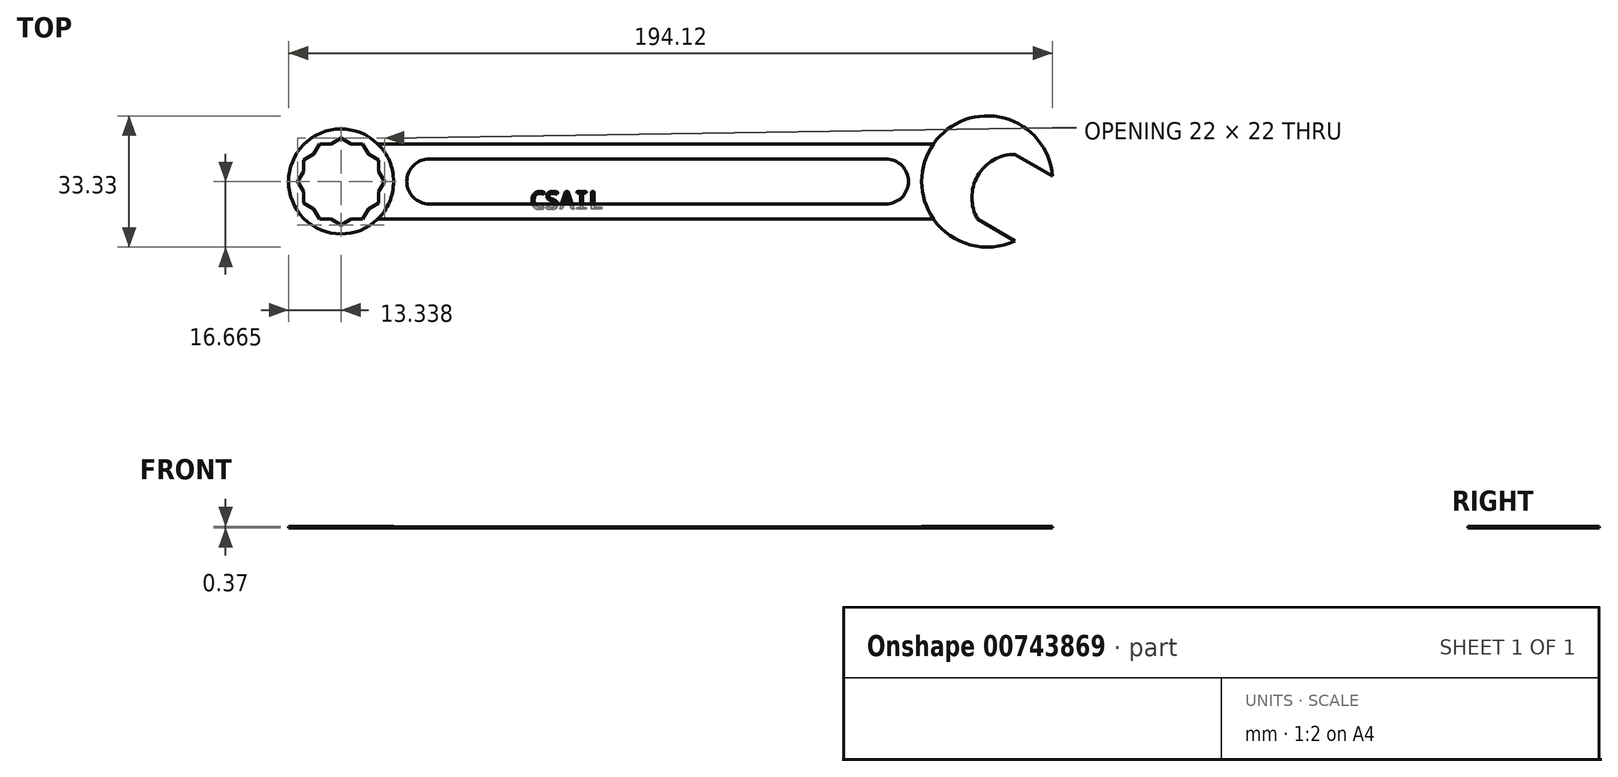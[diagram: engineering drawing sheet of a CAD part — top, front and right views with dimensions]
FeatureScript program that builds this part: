
annotation { "Feature Type Name" : "Feature", "Feature Type Description" : "" }
export const myFeature = defineFeature(function(context is Context, id is Id, definition is map)
    precondition{}
    {
        {
            assignVariable(context, id + "F0", {"name" : "handlethickness", "anyValue" : 1 / 4});
        }
        {
            assignVariable(context, id + "F1", {"name" : "wrenchthick", "anyValue" : 1 / 8});
        }
        {
            assignVariable(context, id + "F2", {"name" : "slotdepth", "anyValue" : .15});
        }
        {
            var Q0;
            Q0=qCreatedBy(makeId("Top.planeOp"),FACE);
            var sketch = newSketch(context, id + "F3", { "sketchPlane" : qUnion([Q0])});
            skLineSegment(sketch, "E0.bottom", {"start": v(0, 0) * mm, "end": v(152.4, 0) * mm});
            skLineSegment(sketch, "E0.top", {"start": v(0, 19.05) * mm, "end": v(152.4, 19.05) * mm});
            skLineSegment(sketch, "E0.left", {"start": v(0, 0) * mm, "end": v(0, 19.05) * mm});
            skLineSegment(sketch, "E0.right", {"start": v(152.4, 0) * mm, "end": v(152.4, 19.05) * mm});
            skSolve(sketch);
        }
        {
            var Q0;
            Q0=makeQuery(id+"F3.imprint","IMPRINT",FACE,{"disambiguationData":[TD([[makeQuery(id+"F3.imprint","IMPRINT",EDGE,{"derivedFrom":sQuery(id+"F3.wireOp",EDGE,"E0.bottom")}),1.0]])]});
            extrude(context, id + "F4", {"entities" : qUnion([Q0]), "flatOperationType" : FlatOperationType.REMOVE, "depth" : (getVariable(context, 'handlethickness')) * mm, "offsetDistance" : 25.4 * mm, "domain" : OperationDomain.MODEL});
        }
        {
            var Q0;
            Q0=makeQuery(id+"F4.opExtrude","CAP_FACE",FACE,{"disambiguationData":[OSD([sQuery(id+"F3.wireOp",EDGE,"E0.bottom"),sQuery(id+"F3.wireOp",EDGE,"E0.top"),sQuery(id+"F3.wireOp",EDGE,"E0.left"),sQuery(id+"F3.wireOp",EDGE,"E0.right")])],"isStart":false});
            var Q1;
            Q1=makeQuery(id+"F4.opExtrude","CAP_FACE",FACE,{"disambiguationData":[OSD([sQuery(id+"F3.wireOp",EDGE,"E0.bottom"),sQuery(id+"F3.wireOp",EDGE,"E0.top"),sQuery(id+"F3.wireOp",EDGE,"E0.left"),sQuery(id+"F3.wireOp",EDGE,"E0.right")])],"isStart":true});
            cPlane(context, id + "F5", {"entities" : qUnion([Q0, Q1]), "cplaneType" : CPlaneType.MID_PLANE, "offset" : 25.4 * mm, "width" : 152.4 * mm, "height" : 152.4 * mm});
        }
        {
            var Q0;
            Q0=qCreatedBy(id+"F5.planeOp",FACE);
            var sketch = newSketch(context, id + "F6", { "sketchPlane" : qUnion([Q0])});
            skPoint(sketch, "E1.0", {"position": v(152.4, 19.05) * mm});
            skCircle(sketch, "E2", {"center": v(154.84, 9.53) * mm, "radius": 16.67 * mm});
            skPoint(sketch, "E2.third.point", {"position": v(171.32, 7.01) * mm});
            skCircle(sketch, "E3.cCircle", {"center": v(161.93, 5.44) * mm, "radius": 9.53 * mm, "construction": true});
            skLineSegment(sketch, "E3.0", {"start": v(171.45, -0.06) * mm, "end": v(161.92, -5.56) * mm});
            skLineSegment(sketch, "E3.1", {"start": v(161.92, -5.56) * mm, "end": v(152.4, -0.06) * mm});
            skLineSegment(sketch, "E3.2", {"start": v(152.4, -0.06) * mm, "end": v(152.4, 10.93) * mm});
            skLineSegment(sketch, "E3.3", {"start": v(152.4, 10.93) * mm, "end": v(161.93, 16.43) * mm});
            skLineSegment(sketch, "E3.4", {"start": v(161.93, 16.43) * mm, "end": v(171.45, 10.93) * mm});
            skLineSegment(sketch, "E3.5", {"start": v(171.45, 10.93) * mm, "end": v(171.45, -0.06) * mm});
            skPoint(sketch, "E3.0.midPoint", {"position": v(166.69, -2.81) * mm});
            skPoint(sketch, "E4.0", {"position": v(152.4, 9.53) * mm});
            skArc(sketch, "E5", {"start": v(161.93, 16.43) * mm, "mid": v(152.4, 10.93) * mm, "end": v(152.4, -0.06) * mm});
            skLineSegment(sketch, "E6.0.1", {"start": v(0, 19.05) * mm, "end": v(0, 0) * mm, "construction": true});
            skPoint(sketch, "E7", {"position": v(141.16, 0) * mm});
            skPoint(sketch, "E8", {"position": v(139.1, 4.06) * mm});
            skPoint(sketch, "E9.0", {"position": v(152.4, 0) * mm});
            skLineSegment(sketch, "E10.0", {"start": v(152.4, 0) * mm, "end": v(152.4, 19.05) * mm, "construction": true});
            skSolve(sketch);
        }
        {
            var Q0;
            {var subQ5=sQuery(id+"F6.wireOp",EDGE,"E3.1");Q0=makeQuery(id+"F6.imprint","IMPRINT",FACE,{"disambiguationData":[TD([[makeQuery(id+"F6.imprint","IMPRINT",EDGE,{"derivedFrom":subQ5}),1.0]])]});}
            extrude(context, id + "F7", {"entities" : qUnion([Q0]), "operationType" : NewBodyOperationType.ADD, "depth" : (getVariable(context, 'handlethickness') + getVariable(context, 'wrenchthick')) * mm, "offsetDistance" : 25.4 * mm, "symmetric" : true});
        }
        {
            var Q0;
            Q0=qCreatedBy(id+"F5.planeOp",FACE);
            var sketch = newSketch(context, id + "F8", { "sketchPlane" : qUnion([Q0])});
            skPoint(sketch, "E11.0", {"position": v(0, 19.05) * mm});
            skPoint(sketch, "E12.0", {"position": v(0, 0) * mm});
            skPoint(sketch, "E13.0", {"position": v(0, 9.53) * mm});
            skCircle(sketch, "E14", {"center": v(-9.33, 9.53) * mm, "radius": 13.33 * mm});
            skPoint(sketch, "E14.third.point", {"position": v(-17.92, 19.72) * mm});
            skCircle(sketch, "E15.cCircle", {"center": v(-9.33, 9.53) * mm, "radius": 9.53 * mm, "construction": true});
            skLineSegment(sketch, "E15.0", {"start": v(-20.33, 9.53) * mm, "end": v(-14.83, 19.05) * mm});
            skLineSegment(sketch, "E15.1", {"start": v(-14.83, 19.05) * mm, "end": v(-3.83, 19.05) * mm});
            skLineSegment(sketch, "E15.2", {"start": v(-3.83, 19.05) * mm, "end": v(1.67, 9.53) * mm});
            skLineSegment(sketch, "E15.3", {"start": v(1.67, 9.53) * mm, "end": v(-3.83, 0) * mm});
            skLineSegment(sketch, "E15.4", {"start": v(-3.83, 0) * mm, "end": v(-14.83, 0) * mm});
            skLineSegment(sketch, "E15.5", {"start": v(-14.83, 0) * mm, "end": v(-20.33, 9.53) * mm});
            skPoint(sketch, "E15.0.midPoint", {"position": v(-17.58, 14.29) * mm});
            skLineSegment(sketch, "E16.0", {"start": v(-9.33, 20.52) * mm, "end": v(0.2, 15.02) * mm});
            skLineSegment(sketch, "E16.1", {"start": v(0.2, 15.02) * mm, "end": v(0.2, 4.03) * mm});
            skLineSegment(sketch, "E16.2", {"start": v(0.2, 4.03) * mm, "end": v(-9.33, -1.47) * mm});
            skLineSegment(sketch, "E16.3", {"start": v(-9.33, -1.47) * mm, "end": v(-18.86, 4.03) * mm});
            skLineSegment(sketch, "E16.4", {"start": v(-18.86, 4.03) * mm, "end": v(-18.86, 15.02) * mm});
            skLineSegment(sketch, "E16.5", {"start": v(-18.86, 15.02) * mm, "end": v(-9.33, 20.52) * mm});
            skPoint(sketch, "E16.0.midPoint", {"position": v(-4.57, 17.77) * mm});
            skSolve(sketch);
        }
        {
            var Q0;
            Q0 = qSketchRegion(id + "F8", true);
            extrude(context, id + "F9", {"entities" : qUnion([Q0]), "operationType" : NewBodyOperationType.ADD, "depth" : (getVariable(context, 'wrenchthick') + getVariable(context, 'handlethickness')) * mm, "offsetDistance" : 25.4 * mm, "symmetric" : true});
        }
        {
            var Q0;
            {var subQ0=sQuery(id+"F3.wireOp",EDGE,"E0.bottom");var subQ1=sQuery(id+"F3.wireOp",EDGE,"E0.top");Q0=makeQuery(id+"F9.boolean.opBoolean","SPLIT",FACE,{"disambiguationData":[TD([makeQuery(id+"F4.opExtrude","SWEPT_FACE",FACE,{"disambiguationData":[OSD([subQ0])]})])],"derivedFrom":makeQuery(id+"F4.opExtrude","CAP_FACE",FACE,{"disambiguationData":[OSD([subQ0,subQ1,sQuery(id+"F3.wireOp",EDGE,"E0.left"),sQuery(id+"F3.wireOp",EDGE,"E0.right")])],"isStart":false})});}
            var sketch = newSketch(context, id + "F10", { "sketchPlane" : qUnion([Q0])});
            skLineSegment(sketch, "E17", {"start": v(4, 9.53) * mm, "end": v(138.17, 9.53) * mm, "construction": true});
            skLineSegment(sketch, "E18.bottom", {"start": v(13.08, 3.81) * mm, "end": v(129.1, 3.81) * mm});
            skLineSegment(sketch, "E18.top", {"start": v(13.08, 15.24) * mm, "end": v(129.1, 15.24) * mm});
            skLineSegment(sketch, "E18.left", {"start": v(13.08, 3.81) * mm, "end": v(13.08, 15.24) * mm});
            skLineSegment(sketch, "E18.right", {"start": v(129.1, 3.81) * mm, "end": v(129.1, 15.24) * mm});
            skPoint(sketch, "E18.middle", {"position": v(71.09, 9.53) * mm});
            skCircle(sketch, "E19", {"center": v(13.08, 9.53) * mm, "radius": 5.72 * mm});
            skCircle(sketch, "E20", {"center": v(129.1, 9.53) * mm, "radius": 5.71 * mm});
            skSolve(sketch);
        }
        {
            var Q0;
            {var subQ0=sQuery(id+"F10.wireOp",EDGE,"E18.left");Q0=makeQuery(id+"F10.imprint","IMPRINT",FACE,{"disambiguationData":[TD([[makeQuery(id+"F10.imprint","IMPRINT",EDGE,{"derivedFrom":subQ0}),1.0]])]});}
            var Q1;
            {var subQ0=sQuery(id+"F10.wireOp",EDGE,"E18.right");Q1=makeQuery(id+"F10.imprint","IMPRINT",FACE,{"disambiguationData":[TD([[makeQuery(id+"F10.imprint","IMPRINT",EDGE,{"derivedFrom":subQ0}),-1.0]])]});}
            var Q2;
            {var subQ0=sQuery(id+"F10.wireOp",EDGE,"E18.bottom");Q2=makeQuery(id+"F10.imprint","IMPRINT",FACE,{"disambiguationData":[TD([[makeQuery(id+"F10.imprint","IMPRINT",EDGE,{"derivedFrom":subQ0}),1.0]])]});}
            var Q3;
            {var subQ0=sQuery(id+"F10.wireOp",EDGE,"E18.right");Q3=makeQuery(id+"F10.imprint","IMPRINT",FACE,{"disambiguationData":[TD([[makeQuery(id+"F10.imprint","IMPRINT",EDGE,{"derivedFrom":subQ0}),1.0]])]});}
            var Q4;
            {var subQ0=sQuery(id+"F10.wireOp",EDGE,"E18.left");Q4=makeQuery(id+"F10.imprint","IMPRINT",FACE,{"disambiguationData":[TD([[makeQuery(id+"F10.imprint","IMPRINT",EDGE,{"derivedFrom":subQ0}),-1.0]])]});}
            extrude(context, id + "F11", {"entities" : qUnion([Q0, Q1, Q2, Q3, Q4]), "operationType" : NewBodyOperationType.REMOVE, "oppositeDirection" : true, "depth" : (getVariable(context, 'slotdepth')) * mm, "offsetDistance" : 25.4 * mm});
        }
        {
            var Q0;
            Q0=makeQuery(id+"F11.boolean.opBoolean","COPY",FACE,{"derivedFrom":makeQuery(id+"F11.opExtrude","CAP_FACE",FACE,{"disambiguationData":[OSD([sQuery(id+"F10.wireOp",EDGE,"E18.bottom"),sQuery(id+"F10.wireOp",EDGE,"E18.top"),sQuery(id+"F10.wireOp",EDGE,"E19"),sQuery(id+"F10.wireOp",EDGE,"E20")])],"isStart":false})});
            var sketch = newSketch(context, id + "F12", { "sketchPlane" : qUnion([Q0])});
            skText(sketch, "E21", { "text": "CSAIL", "fontName": "DroidSansMono.ttf"});
            skPoint(sketch, "E22.0", {"position": v(71.09, 15.24) * mm});
            skPoint(sketch, "E23.0", {"position": v(134.8, 9.53) * mm});
            skLineSegment(sketch, "E24", {"start": v(49.92, 9.53) * mm, "end": v(92.26, 9.53) * mm, "construction": true});
            const initialGuessF12  = {"E21": [0.03875, 0.00253, 1, 0, 0.00446]};
            skSetInitialGuess(sketch, initialGuessF12);
            skSolve(sketch);
        }
        {
            var Q0;
            Q0 = qSketchRegion(id + "F12", true);
            extrude(context, id + "F13", {"entities" : qUnion([Q0]), "operationType" : NewBodyOperationType.REMOVE, "oppositeDirection" : true, "depth" : (getVariable(context, 'slotdepth') * .2) * mm, "offsetDistance" : 25.4 * mm});
        }
        {
            var Q0;
            Q0=makeQuery(id+"F11.boolean.opBoolean","COPY",EDGE,{"derivedFrom":makeQuery(id+"F11.opExtrude","CAP_EDGE",EDGE,{"disambiguationData":[OSD([sQuery(id+"F10.wireOp",EDGE,"E20")])],"isStart":true})});
            var Q1;
            Q1=makeQuery(id+"F11.boolean.opBoolean","COPY",EDGE,{"derivedFrom":makeQuery(id+"F11.opExtrude","CAP_EDGE",EDGE,{"disambiguationData":[OSD([sQuery(id+"F10.wireOp",EDGE,"E18.top")])],"isStart":true})});
            var Q2;
            Q2=makeQuery(id+"F11.boolean.opBoolean","COPY",EDGE,{"derivedFrom":makeQuery(id+"F11.opExtrude","CAP_EDGE",EDGE,{"disambiguationData":[OSD([sQuery(id+"F10.wireOp",EDGE,"E19")])],"isStart":true})});
            var Q3;
            Q3=makeQuery(id+"F11.boolean.opBoolean","COPY",EDGE,{"derivedFrom":makeQuery(id+"F11.opExtrude","CAP_EDGE",EDGE,{"disambiguationData":[OSD([sQuery(id+"F10.wireOp",EDGE,"E18.bottom")])],"isStart":true})});
            var Q4;
            Q4=makeQuery(id+"F11.boolean.opBoolean","COPY",EDGE,{"derivedFrom":makeQuery(id+"F11.opExtrude","CAP_EDGE",EDGE,{"disambiguationData":[OSD([sQuery(id+"F10.wireOp",EDGE,"E18.bottom")])],"isStart":false})});
            var Q5;
            Q5=makeQuery(id+"F11.boolean.opBoolean","COPY",EDGE,{"derivedFrom":makeQuery(id+"F11.opExtrude","CAP_EDGE",EDGE,{"disambiguationData":[OSD([sQuery(id+"F10.wireOp",EDGE,"E20")])],"isStart":false})});
            var Q6;
            Q6=makeQuery(id+"F11.boolean.opBoolean","COPY",EDGE,{"derivedFrom":makeQuery(id+"F11.opExtrude","CAP_EDGE",EDGE,{"disambiguationData":[OSD([sQuery(id+"F10.wireOp",EDGE,"E19")])],"isStart":false})});
            var Q7;
            Q7=makeQuery(id+"F11.boolean.opBoolean","COPY",EDGE,{"derivedFrom":makeQuery(id+"F11.opExtrude","CAP_EDGE",EDGE,{"disambiguationData":[OSD([sQuery(id+"F10.wireOp",EDGE,"E18.top")])],"isStart":false})});
            fillet(context, id + "F14", {"entities" : qUnion([Q0, Q1, Q2, Q3, Q4, Q5, Q6, Q7]), "radius" : (getVariable(context, 'slotdepth') * .5) * mm, "tangentPropagation" : true, "allowEdgeOverflow" : false});
        }
        {
            var Q0;
            Q0=makeQuery(id+"F4.opExtrude","SWEPT_EDGE",EDGE,{"disambiguationData":[OSD([sQuery(id+"F3.wireOp",EDGE,"E0.bottom"),sQuery(id+"F3.wireOp",EDGE,"E0.left")])]});
            var Q1;
            Q1=makeQuery(id+"F9.boolean.opBoolean","INTERSECT",EDGE,{"derivedFrom":[makeQuery(id+"F4.opExtrude","CAP_FACE",FACE,{"disambiguationData":[OSD([sQuery(id+"F3.wireOp",EDGE,"E0.bottom"),sQuery(id+"F3.wireOp",EDGE,"E0.top"),sQuery(id+"F3.wireOp",EDGE,"E0.left"),sQuery(id+"F3.wireOp",EDGE,"E0.right")])],"isStart":false}),makeQuery(id+"F9.opExtrude","SWEPT_FACE",FACE,{"disambiguationData":[OSD([sQuery(id+"F8.wireOp",EDGE,"E14")])]})]});
            var Q2;
            Q2=makeQuery(id+"F4.opExtrude","SWEPT_EDGE",EDGE,{"disambiguationData":[OSD([sQuery(id+"F3.wireOp",EDGE,"E0.top"),sQuery(id+"F3.wireOp",EDGE,"E0.left")])]});
            var Q3;
            Q3=makeQuery(id+"F4.opExtrude","SWEPT_EDGE",EDGE,{"disambiguationData":[OSD([sQuery(id+"F3.wireOp",EDGE,"E0.top"),sQuery(id+"F3.wireOp",EDGE,"E0.right")])]});
            var Q4;
            Q4=makeQuery(id+"F7.boolean.opBoolean","INTERSECT",EDGE,{"derivedFrom":[makeQuery(id+"F4.opExtrude","CAP_FACE",FACE,{"disambiguationData":[OSD([sQuery(id+"F3.wireOp",EDGE,"E0.bottom"),sQuery(id+"F3.wireOp",EDGE,"E0.top"),sQuery(id+"F3.wireOp",EDGE,"E0.left"),sQuery(id+"F3.wireOp",EDGE,"E0.right")])],"isStart":true}),makeQuery(id+"F7.opExtrude","SWEPT_FACE",FACE,{"disambiguationData":[OSD([sQuery(id+"F6.wireOp",EDGE,"E2")])]})]});
            var Q5;
            Q5=makeQuery(id+"F7.boolean.opBoolean","INTERSECT",EDGE,{"derivedFrom":[makeQuery(id+"F4.opExtrude","CAP_FACE",FACE,{"disambiguationData":[OSD([sQuery(id+"F3.wireOp",EDGE,"E0.bottom"),sQuery(id+"F3.wireOp",EDGE,"E0.top"),sQuery(id+"F3.wireOp",EDGE,"E0.left"),sQuery(id+"F3.wireOp",EDGE,"E0.right")])],"isStart":false}),makeQuery(id+"F7.opExtrude","SWEPT_FACE",FACE,{"disambiguationData":[OSD([sQuery(id+"F6.wireOp",EDGE,"E2")])]})]});
            var Q6;
            Q6=makeQuery(id+"F4.opExtrude","SWEPT_EDGE",EDGE,{"disambiguationData":[OSD([sQuery(id+"F3.wireOp",EDGE,"E0.bottom"),sQuery(id+"F3.wireOp",EDGE,"E0.right")])]});
            var Q7;
            Q7=makeQuery(id+"F9.boolean.opBoolean","INTERSECT",EDGE,{"derivedFrom":[makeQuery(id+"F4.opExtrude","CAP_FACE",FACE,{"disambiguationData":[OSD([sQuery(id+"F3.wireOp",EDGE,"E0.bottom"),sQuery(id+"F3.wireOp",EDGE,"E0.top"),sQuery(id+"F3.wireOp",EDGE,"E0.left"),sQuery(id+"F3.wireOp",EDGE,"E0.right")])],"isStart":true}),makeQuery(id+"F9.opExtrude","SWEPT_FACE",FACE,{"disambiguationData":[OSD([sQuery(id+"F8.wireOp",EDGE,"E14")])]})]});
            var Q8;
            Q8=makeQuery(id+"F7.boolean.opBoolean","INTERSECT",EDGE,{"derivedFrom":[makeQuery(id+"F4.opExtrude","SWEPT_FACE",FACE,{"disambiguationData":[OSD([sQuery(id+"F3.wireOp",EDGE,"E0.bottom")])]}),makeQuery(id+"F7.opExtrude","SWEPT_FACE",FACE,{"disambiguationData":[OSD([sQuery(id+"F6.wireOp",EDGE,"E2")])]})]});
            var Q9;
            Q9=makeQuery(id+"F7.boolean.opBoolean","INTERSECT",EDGE,{"derivedFrom":[makeQuery(id+"F4.opExtrude","SWEPT_FACE",FACE,{"disambiguationData":[OSD([sQuery(id+"F3.wireOp",EDGE,"E0.top")])]}),makeQuery(id+"F7.opExtrude","SWEPT_FACE",FACE,{"disambiguationData":[OSD([sQuery(id+"F6.wireOp",EDGE,"E2")])]})]});
            fillet(context, id + "F15", {"entities" : qUnion([Q0, Q1, Q2, Q3, Q4, Q5, Q6, Q7, Q8, Q9]), "radius" : (getVariable(context, 'handlethickness') / 2) * mm, "tangentPropagation" : true, "allowEdgeOverflow" : false});
        }
        {
            var Q0;
            {var subQ7=sQuery(id+"F3.wireOp",EDGE,"E0.left");Q0=makeQuery(id+"F9.boolean.opBoolean","SPLIT",FACE,{"disambiguationData":[TD([makeQuery(id+"F4.opExtrude","SWEPT_FACE",FACE,{"disambiguationData":[OSD([subQ7])]})])],"derivedFrom":makeQuery(id+"F4.opExtrude","CAP_FACE",FACE,{"disambiguationData":[OSD([sQuery(id+"F3.wireOp",EDGE,"E0.bottom"),sQuery(id+"F3.wireOp",EDGE,"E0.top"),subQ7,sQuery(id+"F3.wireOp",EDGE,"E0.right")])],"isStart":false})});}
            var sketch = newSketch(context, id + "F16", { "sketchPlane" : qUnion([Q0])});
            skLineSegment(sketch, "E25.0.0", {"start": v(0, 15.14) * mm, "end": v(0, 3.91) * mm});
            skLineSegment(sketch, "E25.0.1", {"start": v(0, 3.91) * mm, "end": v(0.2, 4.03) * mm});
            skLineSegment(sketch, "E25.0.2", {"start": v(0.2, 4.03) * mm, "end": v(0.2, 6.97) * mm});
            skLineSegment(sketch, "E25.0.3", {"start": v(0.2, 6.97) * mm, "end": v(1.67, 9.53) * mm});
            skLineSegment(sketch, "E25.0.4", {"start": v(1.67, 9.53) * mm, "end": v(0.2, 12.08) * mm});
            skLineSegment(sketch, "E25.0.5", {"start": v(0.2, 12.08) * mm, "end": v(0.2, 15.02) * mm});
            skLineSegment(sketch, "E25.0.6", {"start": v(0.2, 15.02) * mm, "end": v(0, 15.14) * mm});
            skSolve(sketch);
        }
        {
            var Q0;
            Q0 = qSketchRegion(id + "F16", true);
            extrude(context, id + "F17", {"entities" : qUnion([Q0]), "operationType" : NewBodyOperationType.REMOVE, "endBound" : BoundingType.THROUGH_ALL, "oppositeDirection" : true, "depth" : 25.4 * mm, "offsetDistance" : 25.4 * mm});
        }
        {
            var Q0;
            {var subQ0=sQuery(id+"F3.wireOp",EDGE,"E0.bottom");var subQ1=sQuery(id+"F3.wireOp",EDGE,"E0.right");Q0=makeQuery(id+"F7.boolean.opBoolean","SPLIT",FACE,{"disambiguationData":[TD([makeQuery(id+"F4.opExtrude","SWEPT_FACE",FACE,{"disambiguationData":[OSD([subQ1])]})])],"derivedFrom":makeQuery(id+"F4.opExtrude","CAP_FACE",FACE,{"disambiguationData":[OSD([subQ0,sQuery(id+"F3.wireOp",EDGE,"E0.top"),sQuery(id+"F3.wireOp",EDGE,"E0.left"),subQ1])],"isStart":false})});}
            var sketch = newSketch(context, id + "F18", { "sketchPlane" : qUnion([Q0])});
            skArc(sketch, "E26.0.0", {"start": v(152.36, 0) * mm, "mid": v(150.93, 5.47) * mm, "end": v(152.4, 10.93) * mm});
            skArc(sketch, "E26.0.1", {"start": v(152.36, 0) * mm, "mid": v(152.4, 0.24) * mm, "end": v(152.4, 0.48) * mm});
            skLineSegment(sketch, "E26.0.2", {"start": v(152.4, 0.48) * mm, "end": v(152.4, 10.93) * mm});
            skSolve(sketch);
        }
        {
            var Q0;
            Q0=makeQuery(id+"F18.imprint","IMPRINT",FACE,{"disambiguationData":[TD([[makeQuery(id+"F18.imprint","IMPRINT",EDGE,{"derivedFrom":sQuery(id+"F18.wireOp",EDGE,"E26.0.0")}),-1.0]])]});
            extrude(context, id + "F19", {"entities" : qUnion([Q0]), "operationType" : NewBodyOperationType.REMOVE, "endBound" : BoundingType.THROUGH_ALL, "oppositeDirection" : true, "depth" : 25.4 * mm, "offsetDistance" : 25.4 * mm});
        }
        {
            var Q0;
            Q0=makeQuery(id+"F13.boolean.opBoolean","COPY",EDGE,{"derivedFrom":makeQuery(id+"F13.opExtrude","CAP_EDGE",EDGE,{"disambiguationData":[OSD([sQuery(id+"F12.wireOp",EDGE,"E21.sketch_text.stroke-4")])],"isStart":true})});
            var Q1;
            Q1=makeQuery(id+"F13.boolean.opBoolean","COPY",EDGE,{"derivedFrom":makeQuery(id+"F13.opExtrude","CAP_EDGE",EDGE,{"disambiguationData":[OSD([sQuery(id+"F12.wireOp",EDGE,"E21.sketch_text.stroke-5")])],"isStart":true})});
            var Q2;
            Q2=makeQuery(id+"F13.boolean.opBoolean","COPY",EDGE,{"derivedFrom":makeQuery(id+"F13.opExtrude","CAP_EDGE",EDGE,{"disambiguationData":[OSD([sQuery(id+"F12.wireOp",EDGE,"E21.sketch_text.stroke-6")])],"isStart":false})});
            var Q3;
            Q3=makeQuery(id+"F13.boolean.opBoolean","COPY",EDGE,{"derivedFrom":makeQuery(id+"F13.opExtrude","CAP_EDGE",EDGE,{"disambiguationData":[OSD([sQuery(id+"F12.wireOp",EDGE,"E21.sketch_text.stroke-8")])],"isStart":true})});
            var Q4;
            Q4=makeQuery(id+"F13.boolean.opBoolean","COPY",EDGE,{"derivedFrom":makeQuery(id+"F13.opExtrude","CAP_EDGE",EDGE,{"disambiguationData":[OSD([sQuery(id+"F12.wireOp",EDGE,"E21.sketch_text.stroke-7")])],"isStart":true})});
            var Q5;
            Q5=makeQuery(id+"F13.boolean.opBoolean","COPY",EDGE,{"derivedFrom":makeQuery(id+"F13.opExtrude","CAP_EDGE",EDGE,{"disambiguationData":[OSD([sQuery(id+"F12.wireOp",EDGE,"E21.sketch_text.stroke-9")])],"isStart":true})});
            var Q6;
            Q6=makeQuery(id+"F13.boolean.opBoolean","COPY",EDGE,{"derivedFrom":makeQuery(id+"F13.opExtrude","CAP_EDGE",EDGE,{"disambiguationData":[OSD([sQuery(id+"F12.wireOp",EDGE,"E21.sketch_text.stroke-10")])],"isStart":true})});
            var Q7;
            Q7=makeQuery(id+"F13.boolean.opBoolean","COPY",EDGE,{"derivedFrom":makeQuery(id+"F13.opExtrude","CAP_EDGE",EDGE,{"disambiguationData":[OSD([sQuery(id+"F12.wireOp",EDGE,"E21.sketch_text.stroke-12")])],"isStart":false})});
            var Q8;
            Q8=makeQuery(id+"F13.boolean.opBoolean","COPY",EDGE,{"derivedFrom":makeQuery(id+"F13.opExtrude","CAP_EDGE",EDGE,{"disambiguationData":[OSD([sQuery(id+"F12.wireOp",EDGE,"E21.sketch_text.stroke-11")])],"isStart":true})});
            var Q9;
            Q9=makeQuery(id+"F13.boolean.opBoolean","COPY",EDGE,{"derivedFrom":makeQuery(id+"F13.opExtrude","CAP_EDGE",EDGE,{"disambiguationData":[OSD([sQuery(id+"F12.wireOp",EDGE,"E21.sketch_text.stroke-13")])],"isStart":false})});
            var Q10;
            Q10=makeQuery(id+"F13.boolean.opBoolean","COPY",EDGE,{"derivedFrom":makeQuery(id+"F13.opExtrude","CAP_EDGE",EDGE,{"disambiguationData":[OSD([sQuery(id+"F12.wireOp",EDGE,"E21.sketch_text.stroke-12")])],"isStart":true})});
            var Q11;
            Q11=makeQuery(id+"F13.boolean.opBoolean","COPY",EDGE,{"derivedFrom":makeQuery(id+"F13.opExtrude","CAP_EDGE",EDGE,{"disambiguationData":[OSD([sQuery(id+"F12.wireOp",EDGE,"E21.sketch_text.stroke-13")])],"isStart":true})});
            var Q12;
            Q12=makeQuery(id+"F13.boolean.opBoolean","COPY",EDGE,{"derivedFrom":makeQuery(id+"F13.opExtrude","CAP_EDGE",EDGE,{"disambiguationData":[OSD([sQuery(id+"F12.wireOp",EDGE,"E21.sketch_text.stroke-0")])],"isStart":true})});
            var Q13;
            Q13=makeQuery(id+"F13.boolean.opBoolean","COPY",EDGE,{"derivedFrom":makeQuery(id+"F13.opExtrude","CAP_EDGE",EDGE,{"disambiguationData":[OSD([sQuery(id+"F12.wireOp",EDGE,"E21.sketch_text.stroke-0")])],"isStart":false})});
            var Q14;
            Q14=makeQuery(id+"F13.boolean.opBoolean","COPY",EDGE,{"derivedFrom":makeQuery(id+"F13.opExtrude","CAP_EDGE",EDGE,{"disambiguationData":[OSD([sQuery(id+"F12.wireOp",EDGE,"E21.sketch_text.stroke-1")])],"isStart":true})});
            var Q15;
            Q15=makeQuery(id+"F13.boolean.opBoolean","COPY",EDGE,{"derivedFrom":makeQuery(id+"F13.opExtrude","CAP_EDGE",EDGE,{"disambiguationData":[OSD([sQuery(id+"F12.wireOp",EDGE,"E21.sketch_text.stroke-2")])],"isStart":true})});
            var Q16;
            Q16=makeQuery(id+"F13.boolean.opBoolean","COPY",EDGE,{"derivedFrom":makeQuery(id+"F13.opExtrude","CAP_EDGE",EDGE,{"disambiguationData":[OSD([sQuery(id+"F12.wireOp",EDGE,"E21.sketch_text.stroke-11")])],"isStart":false})});
            var Q17;
            Q17=makeQuery(id+"F13.boolean.opBoolean","COPY",EDGE,{"derivedFrom":makeQuery(id+"F13.opExtrude","CAP_EDGE",EDGE,{"disambiguationData":[OSD([sQuery(id+"F12.wireOp",EDGE,"E21.sketch_text.stroke-10")])],"isStart":false})});
            var Q18;
            Q18=makeQuery(id+"F13.boolean.opBoolean","COPY",EDGE,{"derivedFrom":makeQuery(id+"F13.opExtrude","CAP_EDGE",EDGE,{"disambiguationData":[OSD([sQuery(id+"F12.wireOp",EDGE,"E21.sketch_text.stroke-3")])],"isStart":true})});
            var Q19;
            Q19=makeQuery(id+"F13.boolean.opBoolean","COPY",EDGE,{"derivedFrom":makeQuery(id+"F13.opExtrude","CAP_EDGE",EDGE,{"disambiguationData":[OSD([sQuery(id+"F12.wireOp",EDGE,"E21.sketch_text.stroke-9")])],"isStart":false})});
            var Q20;
            Q20=makeQuery(id+"F13.boolean.opBoolean","COPY",EDGE,{"derivedFrom":makeQuery(id+"F13.opExtrude","CAP_EDGE",EDGE,{"disambiguationData":[OSD([sQuery(id+"F12.wireOp",EDGE,"E21.sketch_text.stroke-5")])],"isStart":false})});
            var Q21;
            Q21=makeQuery(id+"F13.boolean.opBoolean","COPY",EDGE,{"derivedFrom":makeQuery(id+"F13.opExtrude","CAP_EDGE",EDGE,{"disambiguationData":[OSD([sQuery(id+"F12.wireOp",EDGE,"E21.sketch_text.stroke-6")])],"isStart":true})});
            var Q22;
            Q22=makeQuery(id+"F13.boolean.opBoolean","COPY",EDGE,{"derivedFrom":makeQuery(id+"F13.opExtrude","CAP_EDGE",EDGE,{"disambiguationData":[OSD([sQuery(id+"F12.wireOp",EDGE,"E21.sketch_text.stroke-7")])],"isStart":false})});
            var Q23;
            Q23=makeQuery(id+"F13.boolean.opBoolean","COPY",EDGE,{"derivedFrom":makeQuery(id+"F13.opExtrude","CAP_EDGE",EDGE,{"disambiguationData":[OSD([sQuery(id+"F12.wireOp",EDGE,"E21.sketch_text.stroke-4")])],"isStart":false})});
            var Q24;
            Q24=makeQuery(id+"F13.boolean.opBoolean","COPY",EDGE,{"derivedFrom":makeQuery(id+"F13.opExtrude","CAP_EDGE",EDGE,{"disambiguationData":[OSD([sQuery(id+"F12.wireOp",EDGE,"E21.sketch_text.stroke-3")])],"isStart":false})});
            var Q25;
            Q25=makeQuery(id+"F13.boolean.opBoolean","COPY",EDGE,{"derivedFrom":makeQuery(id+"F13.opExtrude","CAP_EDGE",EDGE,{"disambiguationData":[OSD([sQuery(id+"F12.wireOp",EDGE,"E21.sketch_text.stroke-2")])],"isStart":false})});
            var Q26;
            Q26=makeQuery(id+"F13.boolean.opBoolean","COPY",EDGE,{"derivedFrom":makeQuery(id+"F13.opExtrude","CAP_EDGE",EDGE,{"disambiguationData":[OSD([sQuery(id+"F12.wireOp",EDGE,"E21.sketch_text.stroke-1")])],"isStart":false})});
            var Q27;
            Q27=makeQuery(id+"F13.boolean.opBoolean","COPY",EDGE,{"derivedFrom":makeQuery(id+"F13.opExtrude","CAP_EDGE",EDGE,{"disambiguationData":[OSD([sQuery(id+"F12.wireOp",EDGE,"E21.sketch_text.stroke-8")])],"isStart":false})});
            var Q28;
            Q28=makeQuery(id+"F13.boolean.opBoolean","COPY",EDGE,{"derivedFrom":makeQuery(id+"F13.opExtrude","CAP_EDGE",EDGE,{"disambiguationData":[OSD([sQuery(id+"F12.wireOp",EDGE,"E21.sketch_text.stroke-15")])],"isStart":true})});
            var Q29;
            Q29=makeQuery(id+"F13.boolean.opBoolean","COPY",EDGE,{"derivedFrom":makeQuery(id+"F13.opExtrude","CAP_EDGE",EDGE,{"disambiguationData":[OSD([sQuery(id+"F12.wireOp",EDGE,"E21.sketch_text.stroke-16")])],"isStart":true})});
            var Q30;
            Q30=makeQuery(id+"F13.boolean.opBoolean","COPY",EDGE,{"derivedFrom":makeQuery(id+"F13.opExtrude","CAP_EDGE",EDGE,{"disambiguationData":[OSD([sQuery(id+"F12.wireOp",EDGE,"E21.sketch_text.stroke-15")])],"isStart":false})});
            var Q31;
            Q31=makeQuery(id+"F13.boolean.opBoolean","COPY",EDGE,{"derivedFrom":makeQuery(id+"F13.opExtrude","CAP_EDGE",EDGE,{"disambiguationData":[OSD([sQuery(id+"F12.wireOp",EDGE,"E21.sketch_text.stroke-16")])],"isStart":false})});
            var Q32;
            Q32=makeQuery(id+"F13.boolean.opBoolean","COPY",EDGE,{"derivedFrom":makeQuery(id+"F13.opExtrude","CAP_EDGE",EDGE,{"disambiguationData":[OSD([sQuery(id+"F12.wireOp",EDGE,"E21.sketch_text.stroke-14")])],"isStart":false})});
            var Q33;
            Q33=makeQuery(id+"F13.boolean.opBoolean","COPY",EDGE,{"derivedFrom":makeQuery(id+"F13.opExtrude","CAP_EDGE",EDGE,{"disambiguationData":[OSD([sQuery(id+"F12.wireOp",EDGE,"E21.sketch_text.stroke-14")])],"isStart":true})});
            var Q34;
            Q34=makeQuery(id+"F13.boolean.opBoolean","COPY",EDGE,{"derivedFrom":makeQuery(id+"F13.opExtrude","CAP_EDGE",EDGE,{"disambiguationData":[OSD([sQuery(id+"F12.wireOp",EDGE,"E21.sketch_text.stroke-33")])],"isStart":true})});
            var Q35;
            Q35=makeQuery(id+"F13.boolean.opBoolean","COPY",EDGE,{"derivedFrom":makeQuery(id+"F13.opExtrude","CAP_EDGE",EDGE,{"disambiguationData":[OSD([sQuery(id+"F12.wireOp",EDGE,"E21.sketch_text.stroke-33")])],"isStart":false})});
            var Q36;
            Q36=makeQuery(id+"F13.boolean.opBoolean","COPY",EDGE,{"derivedFrom":makeQuery(id+"F13.opExtrude","CAP_EDGE",EDGE,{"disambiguationData":[OSD([sQuery(id+"F12.wireOp",EDGE,"E21.sketch_text.stroke-32")])],"isStart":false})});
            var Q37;
            Q37=makeQuery(id+"F13.boolean.opBoolean","COPY",EDGE,{"derivedFrom":makeQuery(id+"F13.opExtrude","CAP_EDGE",EDGE,{"disambiguationData":[OSD([sQuery(id+"F12.wireOp",EDGE,"E21.sketch_text.stroke-32")])],"isStart":true})});
            var Q38;
            Q38=makeQuery(id+"F13.boolean.opBoolean","COPY",EDGE,{"derivedFrom":makeQuery(id+"F13.opExtrude","CAP_EDGE",EDGE,{"disambiguationData":[OSD([sQuery(id+"F12.wireOp",EDGE,"E21.sketch_text.stroke-31")])],"isStart":true})});
            var Q39;
            Q39=makeQuery(id+"F13.boolean.opBoolean","COPY",EDGE,{"derivedFrom":makeQuery(id+"F13.opExtrude","CAP_EDGE",EDGE,{"disambiguationData":[OSD([sQuery(id+"F12.wireOp",EDGE,"E21.sketch_text.stroke-31")])],"isStart":false})});
            var Q40;
            Q40=makeQuery(id+"F13.boolean.opBoolean","COPY",EDGE,{"derivedFrom":makeQuery(id+"F13.opExtrude","CAP_EDGE",EDGE,{"disambiguationData":[OSD([sQuery(id+"F12.wireOp",EDGE,"E21.sketch_text.stroke-17")])],"isStart":false})});
            var Q41;
            Q41=makeQuery(id+"F13.boolean.opBoolean","COPY",EDGE,{"derivedFrom":makeQuery(id+"F13.opExtrude","CAP_EDGE",EDGE,{"disambiguationData":[OSD([sQuery(id+"F12.wireOp",EDGE,"E21.sketch_text.stroke-17")])],"isStart":true})});
            var Q42;
            Q42=makeQuery(id+"F13.boolean.opBoolean","COPY",EDGE,{"derivedFrom":makeQuery(id+"F13.opExtrude","CAP_EDGE",EDGE,{"disambiguationData":[OSD([sQuery(id+"F12.wireOp",EDGE,"E21.sketch_text.stroke-30")])],"isStart":true})});
            var Q43;
            Q43=makeQuery(id+"F13.boolean.opBoolean","COPY",EDGE,{"derivedFrom":makeQuery(id+"F13.opExtrude","CAP_EDGE",EDGE,{"disambiguationData":[OSD([sQuery(id+"F12.wireOp",EDGE,"E21.sketch_text.stroke-30")])],"isStart":false})});
            var Q44;
            Q44=makeQuery(id+"F13.boolean.opBoolean","COPY",EDGE,{"derivedFrom":makeQuery(id+"F13.opExtrude","CAP_EDGE",EDGE,{"disambiguationData":[OSD([sQuery(id+"F12.wireOp",EDGE,"E21.sketch_text.stroke-29")])],"isStart":true})});
            var Q45;
            Q45=makeQuery(id+"F13.boolean.opBoolean","COPY",EDGE,{"derivedFrom":makeQuery(id+"F13.opExtrude","CAP_EDGE",EDGE,{"disambiguationData":[OSD([sQuery(id+"F12.wireOp",EDGE,"E21.sketch_text.stroke-29")])],"isStart":false})});
            var Q46;
            Q46=makeQuery(id+"F13.boolean.opBoolean","COPY",EDGE,{"derivedFrom":makeQuery(id+"F13.opExtrude","CAP_EDGE",EDGE,{"disambiguationData":[OSD([sQuery(id+"F12.wireOp",EDGE,"E21.sketch_text.stroke-28")])],"isStart":false})});
            var Q47;
            Q47=makeQuery(id+"F13.boolean.opBoolean","COPY",EDGE,{"derivedFrom":makeQuery(id+"F13.opExtrude","CAP_EDGE",EDGE,{"disambiguationData":[OSD([sQuery(id+"F12.wireOp",EDGE,"E21.sketch_text.stroke-28")])],"isStart":true})});
            var Q48;
            Q48=makeQuery(id+"F13.boolean.opBoolean","COPY",EDGE,{"derivedFrom":makeQuery(id+"F13.opExtrude","CAP_EDGE",EDGE,{"disambiguationData":[OSD([sQuery(id+"F12.wireOp",EDGE,"E21.sketch_text.stroke-18")])],"isStart":true})});
            var Q49;
            Q49=makeQuery(id+"F13.boolean.opBoolean","COPY",EDGE,{"derivedFrom":makeQuery(id+"F13.opExtrude","CAP_EDGE",EDGE,{"disambiguationData":[OSD([sQuery(id+"F12.wireOp",EDGE,"E21.sketch_text.stroke-18")])],"isStart":false})});
            var Q50;
            Q50=makeQuery(id+"F13.boolean.opBoolean","COPY",EDGE,{"derivedFrom":makeQuery(id+"F13.opExtrude","CAP_EDGE",EDGE,{"disambiguationData":[OSD([sQuery(id+"F12.wireOp",EDGE,"E21.sketch_text.stroke-19")])],"isStart":true})});
            var Q51;
            Q51=makeQuery(id+"F13.boolean.opBoolean","COPY",EDGE,{"derivedFrom":makeQuery(id+"F13.opExtrude","CAP_EDGE",EDGE,{"disambiguationData":[OSD([sQuery(id+"F12.wireOp",EDGE,"E21.sketch_text.stroke-19")])],"isStart":false})});
            var Q52;
            Q52=makeQuery(id+"F13.boolean.opBoolean","COPY",EDGE,{"derivedFrom":makeQuery(id+"F13.opExtrude","CAP_EDGE",EDGE,{"disambiguationData":[OSD([sQuery(id+"F12.wireOp",EDGE,"E21.sketch_text.stroke-20")])],"isStart":true})});
            var Q53;
            Q53=makeQuery(id+"F13.boolean.opBoolean","COPY",EDGE,{"derivedFrom":makeQuery(id+"F13.opExtrude","CAP_EDGE",EDGE,{"disambiguationData":[OSD([sQuery(id+"F12.wireOp",EDGE,"E21.sketch_text.stroke-20")])],"isStart":false})});
            var Q54;
            Q54=makeQuery(id+"F13.boolean.opBoolean","COPY",EDGE,{"derivedFrom":makeQuery(id+"F13.opExtrude","CAP_EDGE",EDGE,{"disambiguationData":[OSD([sQuery(id+"F12.wireOp",EDGE,"E21.sketch_text.stroke-27")])],"isStart":false})});
            var Q55;
            Q55=makeQuery(id+"F13.boolean.opBoolean","COPY",EDGE,{"derivedFrom":makeQuery(id+"F13.opExtrude","CAP_EDGE",EDGE,{"disambiguationData":[OSD([sQuery(id+"F12.wireOp",EDGE,"E21.sketch_text.stroke-27")])],"isStart":true})});
            var Q56;
            Q56=makeQuery(id+"F13.boolean.opBoolean","COPY",EDGE,{"derivedFrom":makeQuery(id+"F13.opExtrude","CAP_EDGE",EDGE,{"disambiguationData":[OSD([sQuery(id+"F12.wireOp",EDGE,"E21.sketch_text.stroke-26")])],"isStart":false})});
            var Q57;
            Q57=makeQuery(id+"F13.boolean.opBoolean","COPY",EDGE,{"derivedFrom":makeQuery(id+"F13.opExtrude","CAP_EDGE",EDGE,{"disambiguationData":[OSD([sQuery(id+"F12.wireOp",EDGE,"E21.sketch_text.stroke-26")])],"isStart":true})});
            var Q58;
            Q58=makeQuery(id+"F13.boolean.opBoolean","COPY",EDGE,{"derivedFrom":makeQuery(id+"F13.opExtrude","CAP_EDGE",EDGE,{"disambiguationData":[OSD([sQuery(id+"F12.wireOp",EDGE,"E21.sketch_text.stroke-24")])],"isStart":false})});
            var Q59;
            Q59=makeQuery(id+"F13.boolean.opBoolean","COPY",EDGE,{"derivedFrom":makeQuery(id+"F13.opExtrude","CAP_EDGE",EDGE,{"disambiguationData":[OSD([sQuery(id+"F12.wireOp",EDGE,"E21.sketch_text.stroke-24")])],"isStart":true})});
            var Q60;
            Q60=makeQuery(id+"F13.boolean.opBoolean","COPY",EDGE,{"derivedFrom":makeQuery(id+"F13.opExtrude","CAP_EDGE",EDGE,{"disambiguationData":[OSD([sQuery(id+"F12.wireOp",EDGE,"E21.sketch_text.stroke-23")])],"isStart":false})});
            var Q61;
            Q61=makeQuery(id+"F13.boolean.opBoolean","COPY",EDGE,{"derivedFrom":makeQuery(id+"F13.opExtrude","CAP_EDGE",EDGE,{"disambiguationData":[OSD([sQuery(id+"F12.wireOp",EDGE,"E21.sketch_text.stroke-22")])],"isStart":false})});
            var Q62;
            Q62=makeQuery(id+"F13.boolean.opBoolean","COPY",EDGE,{"derivedFrom":makeQuery(id+"F13.opExtrude","CAP_EDGE",EDGE,{"disambiguationData":[OSD([sQuery(id+"F12.wireOp",EDGE,"E21.sketch_text.stroke-21")])],"isStart":true})});
            var Q63;
            Q63=makeQuery(id+"F13.boolean.opBoolean","COPY",EDGE,{"derivedFrom":makeQuery(id+"F13.opExtrude","CAP_EDGE",EDGE,{"disambiguationData":[OSD([sQuery(id+"F12.wireOp",EDGE,"E21.sketch_text.stroke-21")])],"isStart":false})});
            var Q64;
            Q64=makeQuery(id+"F13.boolean.opBoolean","COPY",EDGE,{"derivedFrom":makeQuery(id+"F13.opExtrude","CAP_EDGE",EDGE,{"disambiguationData":[OSD([sQuery(id+"F12.wireOp",EDGE,"E21.sketch_text.stroke-25")])],"isStart":true})});
            var Q65;
            Q65=makeQuery(id+"F13.boolean.opBoolean","COPY",EDGE,{"derivedFrom":makeQuery(id+"F13.opExtrude","CAP_EDGE",EDGE,{"disambiguationData":[OSD([sQuery(id+"F12.wireOp",EDGE,"E21.sketch_text.stroke-25")])],"isStart":false})});
            var Q66;
            Q66=makeQuery(id+"F13.boolean.opBoolean","COPY",EDGE,{"derivedFrom":makeQuery(id+"F13.opExtrude","CAP_EDGE",EDGE,{"disambiguationData":[OSD([sQuery(id+"F12.wireOp",EDGE,"E21.sketch_text.stroke-38")])],"isStart":false})});
            var Q67;
            Q67=makeQuery(id+"F13.boolean.opBoolean","COPY",EDGE,{"derivedFrom":makeQuery(id+"F13.opExtrude","CAP_EDGE",EDGE,{"disambiguationData":[OSD([sQuery(id+"F12.wireOp",EDGE,"E21.sketch_text.stroke-38")])],"isStart":true})});
            var Q68;
            Q68=makeQuery(id+"F13.boolean.opBoolean","COPY",EDGE,{"derivedFrom":makeQuery(id+"F13.opExtrude","CAP_EDGE",EDGE,{"disambiguationData":[OSD([sQuery(id+"F12.wireOp",EDGE,"E21.sketch_text.stroke-42")])],"isStart":false})});
            var Q69;
            Q69=makeQuery(id+"F13.boolean.opBoolean","COPY",EDGE,{"derivedFrom":makeQuery(id+"F13.opExtrude","CAP_EDGE",EDGE,{"disambiguationData":[OSD([sQuery(id+"F12.wireOp",EDGE,"E21.sketch_text.stroke-43")])],"isStart":false})});
            var Q70;
            Q70=makeQuery(id+"F13.boolean.opBoolean","COPY",EDGE,{"derivedFrom":makeQuery(id+"F13.opExtrude","CAP_EDGE",EDGE,{"disambiguationData":[OSD([sQuery(id+"F12.wireOp",EDGE,"E21.sketch_text.stroke-43")])],"isStart":true})});
            var Q71;
            Q71=makeQuery(id+"F13.boolean.opBoolean","COPY",EDGE,{"derivedFrom":makeQuery(id+"F13.opExtrude","CAP_EDGE",EDGE,{"disambiguationData":[OSD([sQuery(id+"F12.wireOp",EDGE,"E21.sketch_text.stroke-42")])],"isStart":true})});
            var Q72;
            Q72=makeQuery(id+"F13.boolean.opBoolean","COPY",EDGE,{"derivedFrom":makeQuery(id+"F13.opExtrude","CAP_EDGE",EDGE,{"disambiguationData":[OSD([sQuery(id+"F12.wireOp",EDGE,"E21.sketch_text.stroke-34")])],"isStart":true})});
            var Q73;
            Q73=makeQuery(id+"F13.boolean.opBoolean","COPY",EDGE,{"derivedFrom":makeQuery(id+"F13.opExtrude","CAP_EDGE",EDGE,{"disambiguationData":[OSD([sQuery(id+"F12.wireOp",EDGE,"E21.sketch_text.stroke-34")])],"isStart":false})});
            var Q74;
            Q74=makeQuery(id+"F13.boolean.opBoolean","COPY",EDGE,{"derivedFrom":makeQuery(id+"F13.opExtrude","CAP_EDGE",EDGE,{"disambiguationData":[OSD([sQuery(id+"F12.wireOp",EDGE,"E21.sketch_text.stroke-45")])],"isStart":true})});
            var Q75;
            Q75=makeQuery(id+"F13.boolean.opBoolean","COPY",EDGE,{"derivedFrom":makeQuery(id+"F13.opExtrude","CAP_EDGE",EDGE,{"disambiguationData":[OSD([sQuery(id+"F12.wireOp",EDGE,"E21.sketch_text.stroke-45")])],"isStart":false})});
            var Q76;
            Q76=makeQuery(id+"F13.boolean.opBoolean","COPY",EDGE,{"derivedFrom":makeQuery(id+"F13.opExtrude","CAP_EDGE",EDGE,{"disambiguationData":[OSD([sQuery(id+"F12.wireOp",EDGE,"E21.sketch_text.stroke-44")])],"isStart":true})});
            var Q77;
            Q77=makeQuery(id+"F13.boolean.opBoolean","COPY",EDGE,{"derivedFrom":makeQuery(id+"F13.opExtrude","CAP_EDGE",EDGE,{"disambiguationData":[OSD([sQuery(id+"F12.wireOp",EDGE,"E21.sketch_text.stroke-44")])],"isStart":false})});
            var Q78;
            Q78=makeQuery(id+"F13.boolean.opBoolean","COPY",EDGE,{"derivedFrom":makeQuery(id+"F13.opExtrude","CAP_EDGE",EDGE,{"disambiguationData":[OSD([sQuery(id+"F12.wireOp",EDGE,"E21.sketch_text.stroke-46")])],"isStart":false})});
            var Q79;
            Q79=makeQuery(id+"F13.boolean.opBoolean","COPY",EDGE,{"derivedFrom":makeQuery(id+"F13.opExtrude","CAP_EDGE",EDGE,{"disambiguationData":[OSD([sQuery(id+"F12.wireOp",EDGE,"E21.sketch_text.stroke-46")])],"isStart":true})});
            var Q80;
            Q80=makeQuery(id+"F13.boolean.opBoolean","COPY",EDGE,{"derivedFrom":makeQuery(id+"F13.opExtrude","CAP_EDGE",EDGE,{"disambiguationData":[OSD([sQuery(id+"F12.wireOp",EDGE,"E21.sketch_text.stroke-37")])],"isStart":false})});
            var Q81;
            Q81=makeQuery(id+"F13.boolean.opBoolean","COPY",EDGE,{"derivedFrom":makeQuery(id+"F13.opExtrude","CAP_EDGE",EDGE,{"disambiguationData":[OSD([sQuery(id+"F12.wireOp",EDGE,"E21.sketch_text.stroke-37")])],"isStart":true})});
            var Q82;
            Q82=makeQuery(id+"F13.boolean.opBoolean","COPY",EDGE,{"derivedFrom":makeQuery(id+"F13.opExtrude","CAP_EDGE",EDGE,{"disambiguationData":[OSD([sQuery(id+"F12.wireOp",EDGE,"E21.sketch_text.stroke-35")])],"isStart":false})});
            var Q83;
            Q83=makeQuery(id+"F13.boolean.opBoolean","COPY",EDGE,{"derivedFrom":makeQuery(id+"F13.opExtrude","CAP_EDGE",EDGE,{"disambiguationData":[OSD([sQuery(id+"F12.wireOp",EDGE,"E21.sketch_text.stroke-35")])],"isStart":true})});
            var Q84;
            Q84=makeQuery(id+"F13.boolean.opBoolean","COPY",EDGE,{"derivedFrom":makeQuery(id+"F13.opExtrude","CAP_EDGE",EDGE,{"disambiguationData":[OSD([sQuery(id+"F12.wireOp",EDGE,"E21.sketch_text.stroke-36")])],"isStart":true})});
            var Q85;
            Q85=makeQuery(id+"F13.boolean.opBoolean","COPY",EDGE,{"derivedFrom":makeQuery(id+"F13.opExtrude","CAP_EDGE",EDGE,{"disambiguationData":[OSD([sQuery(id+"F12.wireOp",EDGE,"E21.sketch_text.stroke-36")])],"isStart":false})});
            var Q86;
            Q86=makeQuery(id+"F13.boolean.opBoolean","COPY",EDGE,{"derivedFrom":makeQuery(id+"F13.opExtrude","CAP_EDGE",EDGE,{"disambiguationData":[OSD([sQuery(id+"F12.wireOp",EDGE,"E21.sketch_text.stroke-41")])],"isStart":false})});
            var Q87;
            Q87=makeQuery(id+"F13.boolean.opBoolean","COPY",EDGE,{"derivedFrom":makeQuery(id+"F13.opExtrude","CAP_EDGE",EDGE,{"disambiguationData":[OSD([sQuery(id+"F12.wireOp",EDGE,"E21.sketch_text.stroke-41")])],"isStart":true})});
            var Q88;
            Q88=makeQuery(id+"F13.boolean.opBoolean","COPY",EDGE,{"derivedFrom":makeQuery(id+"F13.opExtrude","CAP_EDGE",EDGE,{"disambiguationData":[OSD([sQuery(id+"F12.wireOp",EDGE,"E21.sketch_text.stroke-40")])],"isStart":false})});
            var Q89;
            Q89=makeQuery(id+"F13.boolean.opBoolean","COPY",EDGE,{"derivedFrom":makeQuery(id+"F13.opExtrude","CAP_EDGE",EDGE,{"disambiguationData":[OSD([sQuery(id+"F12.wireOp",EDGE,"E21.sketch_text.stroke-40")])],"isStart":true})});
            var Q90;
            Q90=makeQuery(id+"F13.boolean.opBoolean","COPY",EDGE,{"derivedFrom":makeQuery(id+"F13.opExtrude","CAP_EDGE",EDGE,{"disambiguationData":[OSD([sQuery(id+"F12.wireOp",EDGE,"E21.sketch_text.stroke-39")])],"isStart":true})});
            var Q91;
            Q91=makeQuery(id+"F13.boolean.opBoolean","COPY",EDGE,{"derivedFrom":makeQuery(id+"F13.opExtrude","CAP_EDGE",EDGE,{"disambiguationData":[OSD([sQuery(id+"F12.wireOp",EDGE,"E21.sketch_text.stroke-39")])],"isStart":false})});
            var Q92;
            Q92=makeQuery(id+"F13.boolean.opBoolean","COPY",EDGE,{"derivedFrom":makeQuery(id+"F13.opExtrude","CAP_EDGE",EDGE,{"disambiguationData":[OSD([sQuery(id+"F12.wireOp",EDGE,"E21.sketch_text.stroke-50")])],"isStart":true})});
            var Q93;
            Q93=makeQuery(id+"F13.boolean.opBoolean","COPY",EDGE,{"derivedFrom":makeQuery(id+"F13.opExtrude","CAP_EDGE",EDGE,{"disambiguationData":[OSD([sQuery(id+"F12.wireOp",EDGE,"E21.sketch_text.stroke-50")])],"isStart":false})});
            var Q94;
            Q94=makeQuery(id+"F13.boolean.opBoolean","COPY",EDGE,{"derivedFrom":makeQuery(id+"F13.opExtrude","CAP_EDGE",EDGE,{"disambiguationData":[OSD([sQuery(id+"F12.wireOp",EDGE,"E21.sketch_text.stroke-49")])],"isStart":true})});
            var Q95;
            Q95=makeQuery(id+"F13.boolean.opBoolean","COPY",EDGE,{"derivedFrom":makeQuery(id+"F13.opExtrude","CAP_EDGE",EDGE,{"disambiguationData":[OSD([sQuery(id+"F12.wireOp",EDGE,"E21.sketch_text.stroke-49")])],"isStart":false})});
            var Q96;
            Q96=makeQuery(id+"F13.boolean.opBoolean","COPY",EDGE,{"derivedFrom":makeQuery(id+"F13.opExtrude","CAP_EDGE",EDGE,{"disambiguationData":[OSD([sQuery(id+"F12.wireOp",EDGE,"E21.sketch_text.stroke-48")])],"isStart":false})});
            var Q97;
            Q97=makeQuery(id+"F13.boolean.opBoolean","COPY",EDGE,{"derivedFrom":makeQuery(id+"F13.opExtrude","CAP_EDGE",EDGE,{"disambiguationData":[OSD([sQuery(id+"F12.wireOp",EDGE,"E21.sketch_text.stroke-48")])],"isStart":true})});
            var Q98;
            Q98=makeQuery(id+"F13.boolean.opBoolean","COPY",EDGE,{"derivedFrom":makeQuery(id+"F13.opExtrude","CAP_EDGE",EDGE,{"disambiguationData":[OSD([sQuery(id+"F12.wireOp",EDGE,"E21.sketch_text.stroke-52")])],"isStart":false})});
            var Q99;
            Q99=makeQuery(id+"F13.boolean.opBoolean","COPY",EDGE,{"derivedFrom":makeQuery(id+"F13.opExtrude","CAP_EDGE",EDGE,{"disambiguationData":[OSD([sQuery(id+"F12.wireOp",EDGE,"E21.sketch_text.stroke-52")])],"isStart":true})});
            var Q100;
            Q100=makeQuery(id+"F13.boolean.opBoolean","COPY",EDGE,{"derivedFrom":makeQuery(id+"F13.opExtrude","CAP_EDGE",EDGE,{"disambiguationData":[OSD([sQuery(id+"F12.wireOp",EDGE,"E21.sketch_text.stroke-53")])],"isStart":true})});
            var Q101;
            Q101=makeQuery(id+"F13.boolean.opBoolean","COPY",EDGE,{"derivedFrom":makeQuery(id+"F13.opExtrude","CAP_EDGE",EDGE,{"disambiguationData":[OSD([sQuery(id+"F12.wireOp",EDGE,"E21.sketch_text.stroke-53")])],"isStart":false})});
            var Q102;
            Q102=makeQuery(id+"F13.boolean.opBoolean","COPY",EDGE,{"derivedFrom":makeQuery(id+"F13.opExtrude","CAP_EDGE",EDGE,{"disambiguationData":[OSD([sQuery(id+"F12.wireOp",EDGE,"E21.sketch_text.stroke-51")])],"isStart":true})});
            var Q103;
            Q103=makeQuery(id+"F13.boolean.opBoolean","COPY",EDGE,{"derivedFrom":makeQuery(id+"F13.opExtrude","CAP_EDGE",EDGE,{"disambiguationData":[OSD([sQuery(id+"F12.wireOp",EDGE,"E21.sketch_text.stroke-51")])],"isStart":false})});
            var Q104;
            Q104=makeQuery(id+"F13.boolean.opBoolean","COPY",EDGE,{"derivedFrom":makeQuery(id+"F13.opExtrude","CAP_EDGE",EDGE,{"disambiguationData":[OSD([sQuery(id+"F12.wireOp",EDGE,"E21.sketch_text.stroke-55")])],"isStart":false})});
            var Q105;
            Q105=makeQuery(id+"F13.boolean.opBoolean","COPY",EDGE,{"derivedFrom":makeQuery(id+"F13.opExtrude","CAP_EDGE",EDGE,{"disambiguationData":[OSD([sQuery(id+"F12.wireOp",EDGE,"E21.sketch_text.stroke-55")])],"isStart":true})});
            var Q106;
            Q106=makeQuery(id+"F13.boolean.opBoolean","COPY",EDGE,{"derivedFrom":makeQuery(id+"F13.opExtrude","CAP_EDGE",EDGE,{"disambiguationData":[OSD([sQuery(id+"F12.wireOp",EDGE,"E21.sketch_text.stroke-54")])],"isStart":true})});
            var Q107;
            Q107=makeQuery(id+"F13.boolean.opBoolean","COPY",EDGE,{"derivedFrom":makeQuery(id+"F13.opExtrude","CAP_EDGE",EDGE,{"disambiguationData":[OSD([sQuery(id+"F12.wireOp",EDGE,"E21.sketch_text.stroke-47")])],"isStart":false})});
            var Q108;
            Q108=makeQuery(id+"F13.boolean.opBoolean","COPY",EDGE,{"derivedFrom":makeQuery(id+"F13.opExtrude","CAP_EDGE",EDGE,{"disambiguationData":[OSD([sQuery(id+"F12.wireOp",EDGE,"E21.sketch_text.stroke-47")])],"isStart":true})});
            var Q109;
            Q109=makeQuery(id+"F13.boolean.opBoolean","COPY",EDGE,{"derivedFrom":makeQuery(id+"F13.opExtrude","CAP_EDGE",EDGE,{"disambiguationData":[OSD([sQuery(id+"F12.wireOp",EDGE,"E21.sketch_text.stroke-58")])],"isStart":false})});
            var Q110;
            Q110=makeQuery(id+"F13.boolean.opBoolean","COPY",EDGE,{"derivedFrom":makeQuery(id+"F13.opExtrude","CAP_EDGE",EDGE,{"disambiguationData":[OSD([sQuery(id+"F12.wireOp",EDGE,"E21.sketch_text.stroke-58")])],"isStart":true})});
            var Q111;
            Q111=makeQuery(id+"F13.boolean.opBoolean","COPY",EDGE,{"derivedFrom":makeQuery(id+"F13.opExtrude","CAP_EDGE",EDGE,{"disambiguationData":[OSD([sQuery(id+"F12.wireOp",EDGE,"E21.sketch_text.stroke-57")])],"isStart":false})});
            var Q112;
            Q112=makeQuery(id+"F13.boolean.opBoolean","COPY",EDGE,{"derivedFrom":makeQuery(id+"F13.opExtrude","CAP_EDGE",EDGE,{"disambiguationData":[OSD([sQuery(id+"F12.wireOp",EDGE,"E21.sketch_text.stroke-57")])],"isStart":true})});
            var Q113;
            Q113=makeQuery(id+"F13.boolean.opBoolean","COPY",EDGE,{"derivedFrom":makeQuery(id+"F13.opExtrude","CAP_EDGE",EDGE,{"disambiguationData":[OSD([sQuery(id+"F12.wireOp",EDGE,"E21.sketch_text.stroke-56")])],"isStart":true})});
            var Q114;
            Q114=makeQuery(id+"F13.boolean.opBoolean","COPY",EDGE,{"derivedFrom":makeQuery(id+"F13.opExtrude","CAP_EDGE",EDGE,{"disambiguationData":[OSD([sQuery(id+"F12.wireOp",EDGE,"E21.sketch_text.stroke-56")])],"isStart":false})});
            var Q115;
            Q115=makeQuery(id+"F13.boolean.opBoolean","COPY",EDGE,{"derivedFrom":makeQuery(id+"F13.opExtrude","CAP_EDGE",EDGE,{"disambiguationData":[OSD([sQuery(id+"F12.wireOp",EDGE,"E21.sketch_text.stroke-54")])],"isStart":false})});
            var Q116;
            Q116=makeQuery(id+"F13.boolean.opBoolean","COPY",EDGE,{"derivedFrom":makeQuery(id+"F13.opExtrude","CAP_EDGE",EDGE,{"disambiguationData":[OSD([sQuery(id+"F12.wireOp",EDGE,"E21.sketch_text.stroke-61")])],"isStart":false})});
            var Q117;
            Q117=makeQuery(id+"F13.boolean.opBoolean","COPY",EDGE,{"derivedFrom":makeQuery(id+"F13.opExtrude","CAP_EDGE",EDGE,{"disambiguationData":[OSD([sQuery(id+"F12.wireOp",EDGE,"E21.sketch_text.stroke-61")])],"isStart":true})});
            var Q118;
            Q118=makeQuery(id+"F13.boolean.opBoolean","COPY",EDGE,{"derivedFrom":makeQuery(id+"F13.opExtrude","CAP_EDGE",EDGE,{"disambiguationData":[OSD([sQuery(id+"F12.wireOp",EDGE,"E21.sketch_text.stroke-62")])],"isStart":false})});
            var Q119;
            Q119=makeQuery(id+"F13.boolean.opBoolean","COPY",EDGE,{"derivedFrom":makeQuery(id+"F13.opExtrude","CAP_EDGE",EDGE,{"disambiguationData":[OSD([sQuery(id+"F12.wireOp",EDGE,"E21.sketch_text.stroke-62")])],"isStart":true})});
            var Q120;
            Q120=makeQuery(id+"F13.boolean.opBoolean","COPY",EDGE,{"derivedFrom":makeQuery(id+"F13.opExtrude","CAP_EDGE",EDGE,{"disambiguationData":[OSD([sQuery(id+"F12.wireOp",EDGE,"E21.sketch_text.stroke-63")])],"isStart":true})});
            var Q121;
            Q121=makeQuery(id+"F13.boolean.opBoolean","COPY",EDGE,{"derivedFrom":makeQuery(id+"F13.opExtrude","CAP_EDGE",EDGE,{"disambiguationData":[OSD([sQuery(id+"F12.wireOp",EDGE,"E21.sketch_text.stroke-63")])],"isStart":false})});
            var Q122;
            Q122=makeQuery(id+"F13.boolean.opBoolean","COPY",EDGE,{"derivedFrom":makeQuery(id+"F13.opExtrude","CAP_EDGE",EDGE,{"disambiguationData":[OSD([sQuery(id+"F12.wireOp",EDGE,"E21.sketch_text.stroke-64")])],"isStart":false})});
            var Q123;
            Q123=makeQuery(id+"F13.boolean.opBoolean","COPY",EDGE,{"derivedFrom":makeQuery(id+"F13.opExtrude","CAP_EDGE",EDGE,{"disambiguationData":[OSD([sQuery(id+"F12.wireOp",EDGE,"E21.sketch_text.stroke-64")])],"isStart":true})});
            var Q124;
            Q124=makeQuery(id+"F13.boolean.opBoolean","COPY",EDGE,{"derivedFrom":makeQuery(id+"F13.opExtrude","CAP_EDGE",EDGE,{"disambiguationData":[OSD([sQuery(id+"F12.wireOp",EDGE,"E21.sketch_text.stroke-59")])],"isStart":true})});
            var Q125;
            Q125=makeQuery(id+"F13.boolean.opBoolean","COPY",EDGE,{"derivedFrom":makeQuery(id+"F13.opExtrude","CAP_EDGE",EDGE,{"disambiguationData":[OSD([sQuery(id+"F12.wireOp",EDGE,"E21.sketch_text.stroke-59")])],"isStart":false})});
            var Q126;
            Q126=makeQuery(id+"F13.boolean.opBoolean","COPY",EDGE,{"derivedFrom":makeQuery(id+"F13.opExtrude","CAP_EDGE",EDGE,{"disambiguationData":[OSD([sQuery(id+"F12.wireOp",EDGE,"E21.sketch_text.stroke-60")])],"isStart":true})});
            var Q127;
            Q127=makeQuery(id+"F13.boolean.opBoolean","COPY",EDGE,{"derivedFrom":makeQuery(id+"F13.opExtrude","CAP_EDGE",EDGE,{"disambiguationData":[OSD([sQuery(id+"F12.wireOp",EDGE,"E21.sketch_text.stroke-60")])],"isStart":false})});
            var Q128;
            Q128=makeQuery(id+"F13.boolean.opBoolean","COPY",EDGE,{"derivedFrom":makeQuery(id+"F13.opExtrude","CAP_EDGE",EDGE,{"disambiguationData":[OSD([sQuery(id+"F12.wireOp",EDGE,"E21.sketch_text.stroke-23")])],"isStart":true})});
            var Q129;
            Q129=makeQuery(id+"F13.boolean.opBoolean","COPY",EDGE,{"derivedFrom":makeQuery(id+"F13.opExtrude","CAP_EDGE",EDGE,{"disambiguationData":[OSD([sQuery(id+"F12.wireOp",EDGE,"E21.sketch_text.stroke-22")])],"isStart":true})});
            fillet(context, id + "F20", {"entities" : qUnion([Q0, Q1, Q2, Q3, Q4, Q5, Q6, Q7, Q8, Q9, Q10, Q11, Q12, Q13, Q14, Q15, Q16, Q17, Q18, Q19, Q20, Q21, Q22, Q23, Q24, Q25, Q26, Q27, Q28, Q29, Q30, Q31, Q32, Q33, Q34, Q35, Q36, Q37, Q38, Q39, Q40, Q41, Q42, Q43, Q44, Q45, Q46, Q47, Q48, Q49, Q50, Q51, Q52, Q53, Q54, Q55, Q56, Q57, Q58, Q59, Q60, Q61, Q62, Q63, Q64, Q65, Q66, Q67, Q68, Q69, Q70, Q71, Q72, Q73, Q74, Q75, Q76, Q77, Q78, Q79, Q80, Q81, Q82, Q83, Q84, Q85, Q86, Q87, Q88, Q89, Q90, Q91, Q92, Q93, Q94, Q95, Q96, Q97, Q98, Q99, Q100, Q101, Q102, Q103, Q104, Q105, Q106, Q107, Q108, Q109, Q110, Q111, Q112, Q113, Q114, Q115, Q116, Q117, Q118, Q119, Q120, Q121, Q122, Q123, Q124, Q125, Q126, Q127, Q128, Q129]), "radius" : (getVariable(context, 'slotdepth') * .1) * mm, "tangentPropagation" : true, "allowEdgeOverflow" : false});
        }
        {
            var Q0;
            Q0=makeQuery(id+"F4.opExtrude","SWEPT_FACE",FACE,{"disambiguationData":[OSD([sQuery(id+"F3.wireOp",EDGE,"E0.top")])]});
            var Q1;
            {var subQ1=sQuery(id+"F3.wireOp",EDGE,"E0.left");var subQ3=sQuery(id+"F3.wireOp",EDGE,"E0.bottom");Q1=makeQuery(id+"F7.boolean.opBoolean","SPLIT",FACE,{"disambiguationData":[TD([makeQuery(id+"F4.opExtrude","SWEPT_FACE",FACE,{"disambiguationData":[OSD([subQ1])]})])],"derivedFrom":makeQuery(id+"F4.opExtrude","SWEPT_FACE",FACE,{"disambiguationData":[OSD([subQ3])]})});}
            cPlane(context, id + "F21", {"entities" : qUnion([Q0, Q1]), "cplaneType" : CPlaneType.MID_PLANE, "offset" : 25.4 * mm, "width" : 152.4 * mm, "height" : 152.4 * mm});
        }
        {
            var Q0;
            Q0=qCreatedBy(id+"F21.planeOp",FACE);
            var sketch = newSketch(context, id + "F22", { "sketchPlane" : qUnion([Q0])});
            skPoint(sketch, "E27.0", {"position": v(0, 3.18) * mm});
            skPoint(sketch, "E28.0", {"position": v(-1.67, 3.18) * mm});
            skPoint(sketch, "E29.0", {"position": v(-1.67, 7.94) * mm});
            skPoint(sketch, "E30.0", {"position": v(9.33, 3.18) * mm});
            skPoint(sketch, "E31.0", {"position": v(-1.67, -1.59) * mm});
            skLineSegment(sketch, "E32.bottom", {"start": v(0, 3.18) * mm, "end": v(-1.67, 3.18) * mm, "construction": true});
            skLineSegment(sketch, "E32.top", {"start": v(0, 7.94) * mm, "end": v(-1.67, 7.94) * mm, "construction": true});
            skLineSegment(sketch, "E32.left", {"start": v(0, 3.18) * mm, "end": v(0, 7.94) * mm, "construction": true});
            skLineSegment(sketch, "E32.right", {"start": v(-1.67, 3.18) * mm, "end": v(-1.67, 7.94) * mm, "construction": true});
            skLineSegment(sketch, "E33.top", {"start": v(-1.67, -1.59) * mm, "end": v(0, -1.59) * mm, "construction": true});
            skLineSegment(sketch, "E33.left", {"start": v(-1.67, 3.18) * mm, "end": v(-1.67, -1.59) * mm, "construction": true});
            skLineSegment(sketch, "E33.right", {"start": v(0, 1.59) * mm, "end": v(0, -1.59) * mm, "construction": true});
            skLineSegment(sketch, "E34", {"start": v(-1.67, 7.94) * mm, "end": v(0, 6.27) * mm});
            skLineSegment(sketch, "E35", {"start": v(-1.67, 4.74) * mm, "end": v(-1.67, 5.42) * mm});
            skLineSegment(sketch, "E36", {"start": v(0, 6.27) * mm, "end": v(0, 7.94) * mm});
            skLineSegment(sketch, "E37", {"start": v(-1.67, 7.94) * mm, "end": v(0, 7.94) * mm});
            skLineSegment(sketch, "E38.MirrorCS", {"start": v(-1.67, -1.59) * mm, "end": v(0, 0.08) * mm});
            skLineSegment(sketch, "E39.MirrorCS", {"start": v(0, 3.18) * mm, "end": v(0, -1.59) * mm, "construction": true});
            skLineSegment(sketch, "E40.MirrorCS", {"start": v(0, -1.59) * mm, "end": v(-1.67, -1.59) * mm, "construction": true});
            skLineSegment(sketch, "E41", {"start": v(-1.67, -1.59) * mm, "end": v(0, -1.59) * mm});
            skLineSegment(sketch, "E42", {"start": v(0, 0.08) * mm, "end": v(0, -1.59) * mm});
            skLineSegment(sketch, "E43", {"start": v(9.33, 3.18) * mm, "end": v(9.33, 7.16) * mm, "construction": true});
            skSolve(sketch);
        }
        {
            var Q0;
            Q0 = qSketchRegion(id + "F22", true);
            var Q1;
            Q1=sQuery(id+"F22.wireOp",EDGE,"E43");
            revolve(context, id + "F23", {"operationType" : NewBodyOperationType.REMOVE, "surfaceOperationType" : NewSurfaceOperationType.NEW, "entities" : qUnion([Q0]), "axis" : qUnion([Q1]), "revolveType" : RevolveType.FULL, "oppositeDirection" : true});
        }
    });
